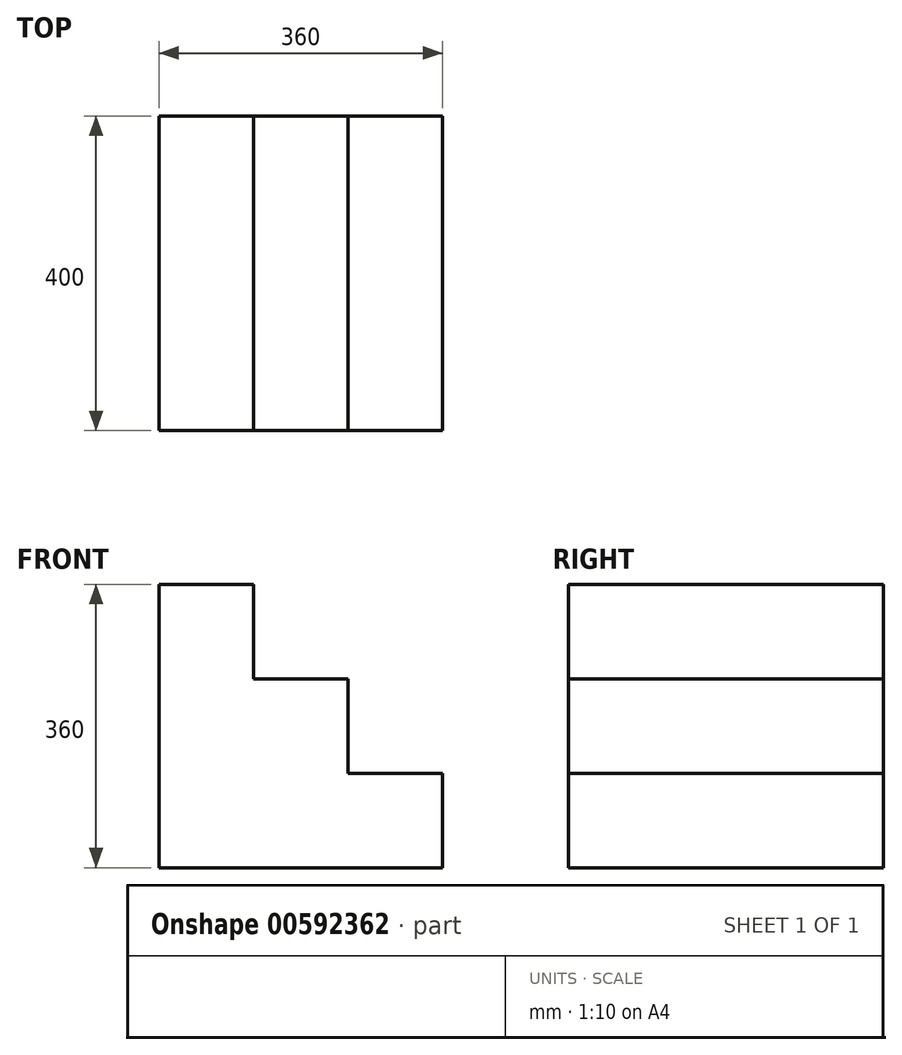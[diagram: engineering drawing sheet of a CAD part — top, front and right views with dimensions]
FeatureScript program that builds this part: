
annotation { "Feature Type Name" : "Feature", "Feature Type Description" : "" }
export const myFeature = defineFeature(function(context is Context, id is Id, definition is map)
    precondition{}
    {
        {
            var Q0;
            Q0=qCreatedBy(makeId("Front.planeOp"),FACE);
            var sketch = newSketch(context, id + "F0", { "sketchPlane" : qUnion([Q0])});
            skLineSegment(sketch, "E0", {"start": v(0, 0) * mm, "end": v(360, 0) * mm});
            skLineSegment(sketch, "E1", {"start": v(0, 0) * mm, "end": v(0, 360) * mm});
            skLineSegment(sketch, "E2", {"start": v(0, 360) * mm, "end": v(120, 360) * mm});
            skLineSegment(sketch, "E3", {"start": v(120, 360) * mm, "end": v(120, 240) * mm});
            skLineSegment(sketch, "E4", {"start": v(120, 240) * mm, "end": v(240, 240) * mm});
            skLineSegment(sketch, "E5", {"start": v(240, 240) * mm, "end": v(240, 120) * mm});
            skLineSegment(sketch, "E6", {"start": v(240, 120) * mm, "end": v(360, 120) * mm});
            skLineSegment(sketch, "E7", {"start": v(360, 120) * mm, "end": v(360, 0) * mm});
            skSolve(sketch);
        }
        {
            var Q0;
            Q0=makeQuery(id+"F0.imprint","IMPRINT",FACE,{"disambiguationData":[TD([[makeQuery(id+"F0.imprint","IMPRINT",EDGE,{"derivedFrom":sQuery(id+"F0.wireOp",EDGE,"E0")}),1.0]])]});
            extrude(context, id + "F1", {"entities" : qUnion([Q0]), "depth" : 400 * mm, "offsetDistance" : 25 * mm});
        }
    });
